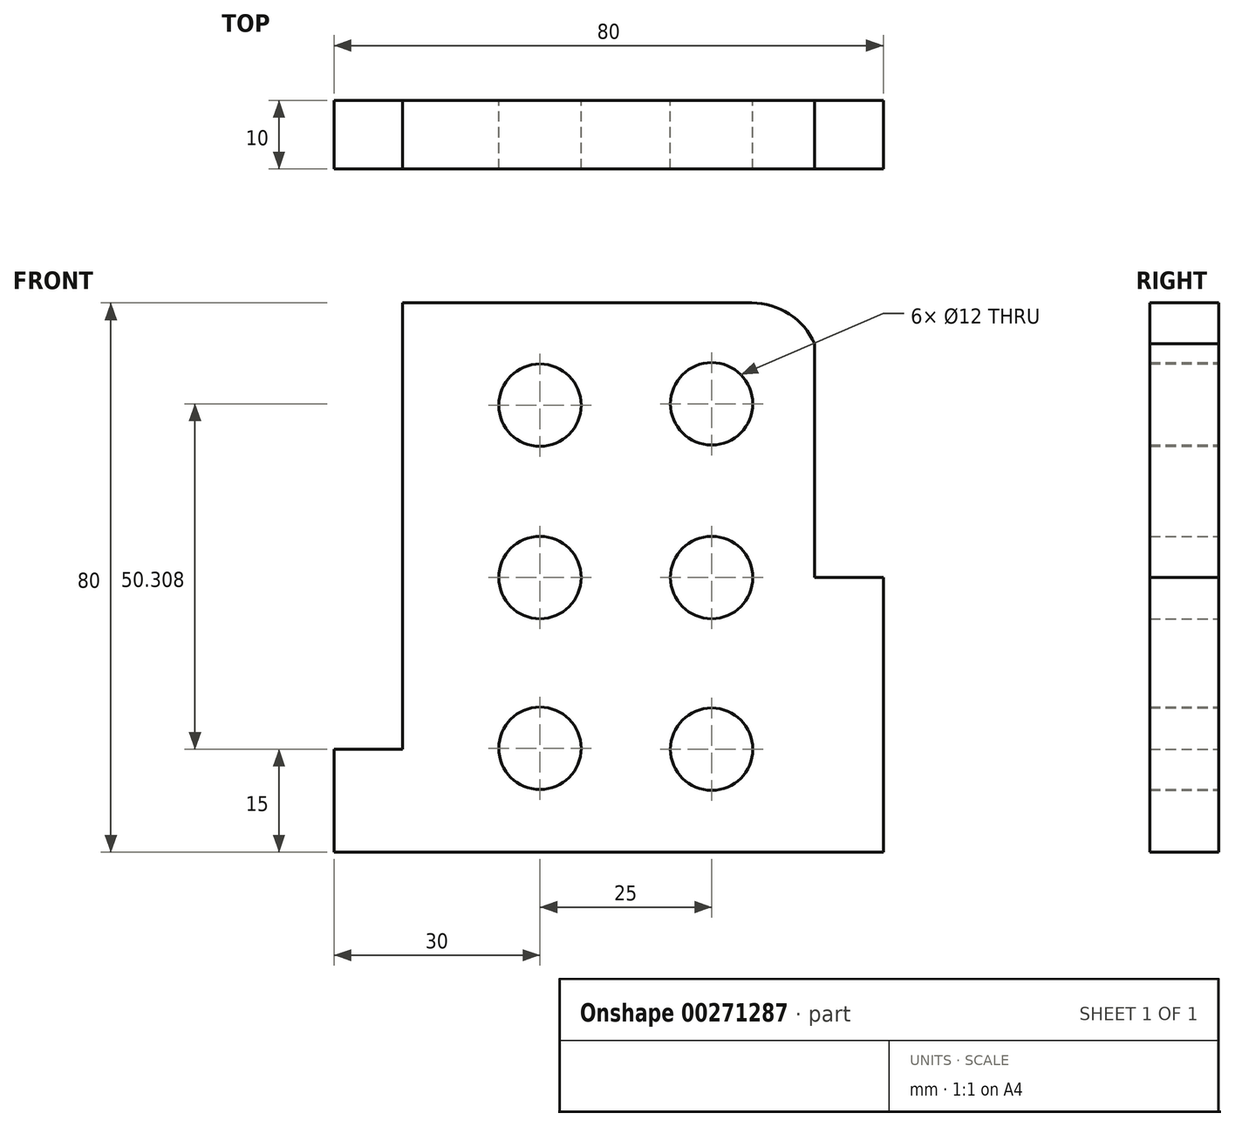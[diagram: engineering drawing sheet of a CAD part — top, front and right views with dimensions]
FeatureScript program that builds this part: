
annotation { "Feature Type Name" : "Feature", "Feature Type Description" : "" }
export const myFeature = defineFeature(function(context is Context, id is Id, definition is map)
    precondition{}
    {
        {
            var Q0;
            Q0=qCreatedBy(makeId("Front.planeOp"),FACE);
            var sketch = newSketch(context, id + "F0", { "sketchPlane" : qUnion([Q0])});
            skLineSegment(sketch, "E0", {"start": v(0, 0) * mm, "end": v(80, 0) * mm});
            skLineSegment(sketch, "E1", {"start": v(80, 0) * mm, "end": v(80, 40) * mm});
            skLineSegment(sketch, "E2", {"start": v(80, 40) * mm, "end": v(70, 40) * mm});
            skLineSegment(sketch, "E3", {"start": v(0, 0) * mm, "end": v(0, 15) * mm});
            skLineSegment(sketch, "E4", {"start": v(0, 15) * mm, "end": v(10, 15) * mm});
            skLineSegment(sketch, "E5", {"start": v(10, 15) * mm, "end": v(10, 80) * mm});
            skLineSegment(sketch, "E6", {"start": v(10, 80) * mm, "end": v(60.86, 80) * mm});
            skLineSegment(sketch, "E7", {"start": v(70, 74.05) * mm, "end": v(70, 40) * mm});
            skLineSegment(sketch, "E8", {"start": v(0, 0) * mm, "end": v(55, 0) * mm});
            skPoint(sketch, "E9", {"position": v(30, 0) * mm});
            skPoint(sketch, "E10", {"position": v(10, 65) * mm});
            skPoint(sketch, "E11", {"position": v(10, 40) * mm});
            skArc(sketch, "E12", {"start": v(60.86, 80) * mm, "mid": v(66.31, 78.38) * mm, "end": v(70, 74.05) * mm});
            skCircle(sketch, "E13", {"center": v(30, 15.14) * mm, "radius": 6 * mm});
            skCircle(sketch, "E14", {"center": v(55, 15) * mm, "radius": 6 * mm});
            skCircle(sketch, "E15", {"center": v(55, 40) * mm, "radius": 6 * mm});
            skCircle(sketch, "E16", {"center": v(30, 40) * mm, "radius": 6 * mm});
            skCircle(sketch, "E17", {"center": v(30, 65.1) * mm, "radius": 6 * mm});
            skCircle(sketch, "E18", {"center": v(55, 65.3) * mm, "radius": 6 * mm});
            skSolve(sketch);
        }
        {
            var Q0;
            Q0 = qSketchRegion(id + "F0", true);
            extrude(context, id + "F1", {"entities" : qUnion([Q0]), "depth" : 10 * mm});
        }
    });
